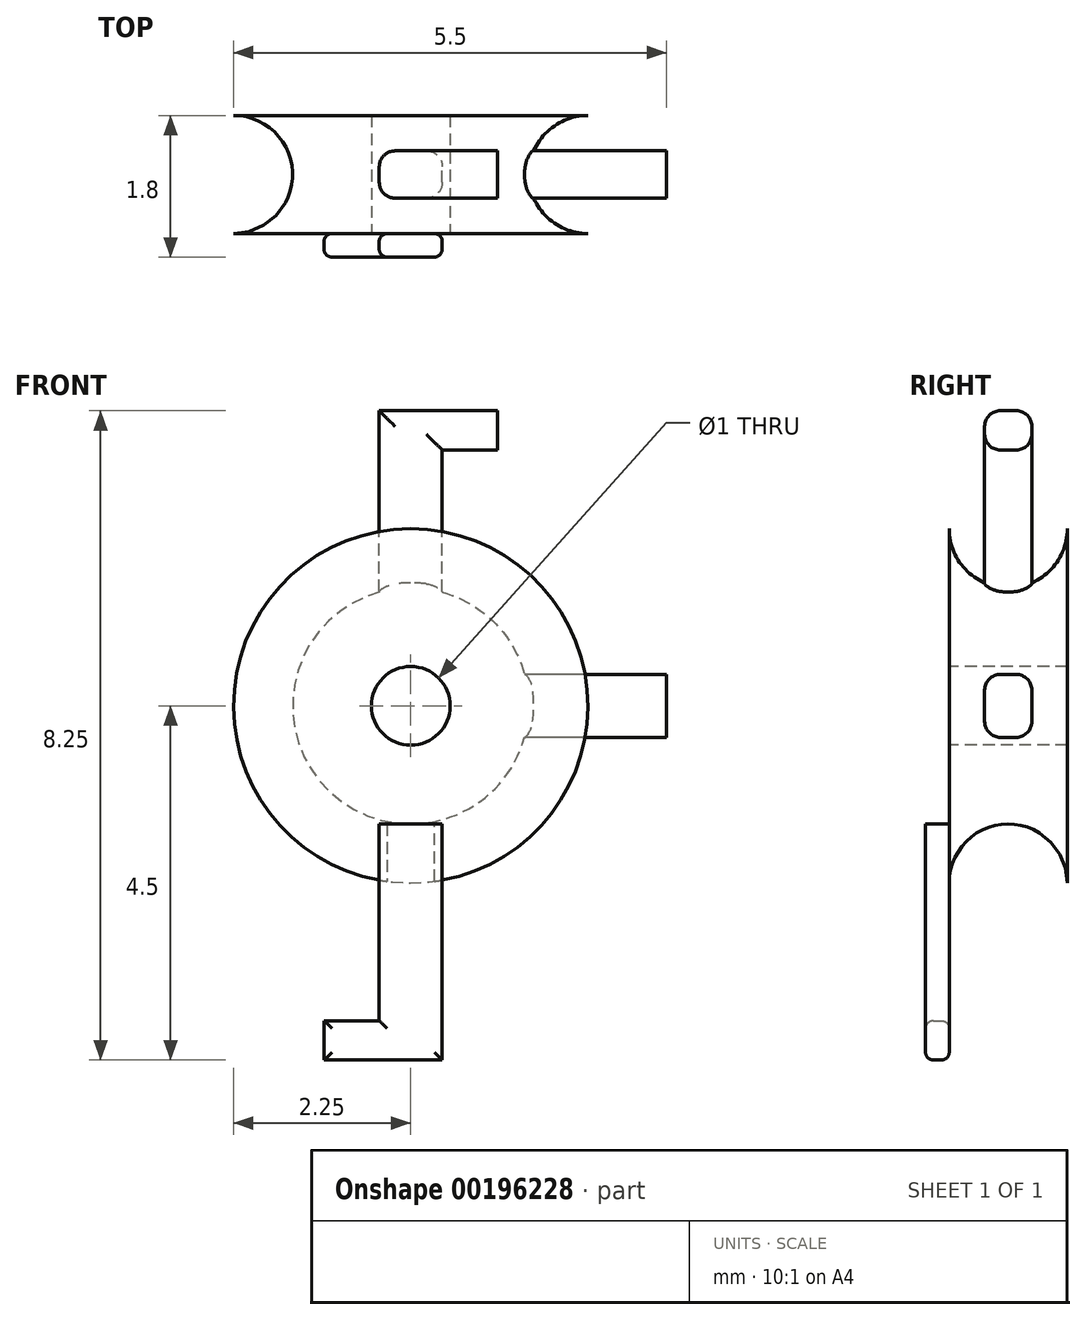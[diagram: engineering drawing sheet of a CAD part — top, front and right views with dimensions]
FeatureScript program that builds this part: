
annotation { "Feature Type Name" : "Feature", "Feature Type Description" : "" }
export const myFeature = defineFeature(function(context is Context, id is Id, definition is map)
    precondition{}
    {
        {
            var Q0;
            Q0=qCreatedBy(makeId("Front.planeOp"),FACE);
            var sketch = newSketch(context, id + "F0", { "sketchPlane" : qUnion([Q0])});
            skCircle(sketch, "E0", {"center": v(0, 0) * mm, "radius": 2.25 * mm});
            skSolve(sketch);
        }
        {
            var Q0;
            Q0 = qSketchRegion(id + "F0", true);
            extrude(context, id + "F1", {"entities" : qUnion([Q0]), "depth" : 1.5 * mm});
        }
        {
            var Q0;
            Q0=qCreatedBy(makeId("Top.planeOp"),FACE);
            var sketch = newSketch(context, id + "F2", { "sketchPlane" : qUnion([Q0])});
            skLineSegment(sketch, "E1", {"start": v(-2.25, -1.5) * mm, "end": v(-2.25, 0) * mm, "construction": true});
            skCircle(sketch, "E2", {"center": v(-2.25, -0.75) * mm, "radius": 0.75 * mm});
            skSolve(sketch);
        }
        {
            var Q0;
            Q0=makeQuery(id+"F2.imprint","IMPRINT",FACE,{"disambiguationData":[TD([[makeQuery(id+"F2.imprint","IMPRINT",EDGE,{"derivedFrom":sQuery(id+"F2.wireOp",EDGE,"E2")}),1.0]])]});
            var Q1;
            Q1=makeQuery(id+"F1.opExtrude","SWEPT_FACE",FACE,{"disambiguationData":[OSD([sQuery(id+"F0.wireOp",EDGE,"E0")])]});
            revolve(context, id + "F3", {"operationType" : NewBodyOperationType.REMOVE, "entities" : qUnion([Q0]), "axis" : qUnion([Q1]), "revolveType" : RevolveType.FULL, "oppositeDirection" : true});
        }
        {
            var Q0;
            Q0=makeQuery(id+"F1.opExtrude","CAP_FACE",FACE,{"disambiguationData":[OSD([sQuery(id+"F0.wireOp",EDGE,"E0")])],"isStart":false});
            var sketch = newSketch(context, id + "F4", { "sketchPlane" : qUnion([Q0])});
            skCircle(sketch, "E3", {"center": v(0, 0) * mm, "radius": 0.5 * mm});
            skSolve(sketch);
        }
        {
            var Q0;
            Q0=makeQuery(id+"F4.imprint","IMPRINT",FACE,{"disambiguationData":[TD([[makeQuery(id+"F4.imprint","IMPRINT",EDGE,{"derivedFrom":sQuery(id+"F4.wireOp",EDGE,"E3")}),1.0]])]});
            extrude(context, id + "F5", {"entities" : qUnion([Q0]), "operationType" : NewBodyOperationType.REMOVE, "oppositeDirection" : true, "depth" : 25 * mm});
        }
        {
            var Q0;
            Q0=qCreatedBy(makeId("Front.planeOp"),FACE);
            cPlane(context, id + "F6", {"entities" : qUnion([Q0]), "cplaneType" : CPlaneType.OFFSET, "offset" : 0.75 * mm, "width" : 150 * mm, "height" : 150 * mm});
        }
        {
            var Q0;
            Q0=qCreatedBy(id+"F6.planeOp",FACE);
            var sketch = newSketch(context, id + "F7", { "sketchPlane" : qUnion([Q0])});
            skLineSegment(sketch, "E4.bottom", {"start": v(0.4, 0.75) * mm, "end": v(-0.4, 0.75) * mm});
            skLineSegment(sketch, "E4.top", {"start": v(0.4, 3.75) * mm, "end": v(-0.4, 3.75) * mm});
            skLineSegment(sketch, "E4.left", {"start": v(0.4, 0.75) * mm, "end": v(0.4, 3.25) * mm});
            skLineSegment(sketch, "E4.right", {"start": v(-0.4, 0.75) * mm, "end": v(-0.4, 3.75) * mm});
            skPoint(sketch, "E4.middle", {"position": v(0, 2.25) * mm});
            skLineSegment(sketch, "E5", {"start": v(0.4, 3.75) * mm, "end": v(1.1, 3.75) * mm});
            skLineSegment(sketch, "E6", {"start": v(1.1, 3.75) * mm, "end": v(1.1, 3.25) * mm});
            skLineSegment(sketch, "E7", {"start": v(1.1, 3.25) * mm, "end": v(0.4, 3.25) * mm});
            skSolve(sketch);
        }
        {
            var Q0;
            Q0 = qSketchRegion(id + "F7", true);
            extrude(context, id + "F8", {"entities" : qUnion([Q0]), "operationType" : NewBodyOperationType.ADD, "depth" : 0.3 * mm, "hasSecondDirection" : true, "secondDirectionOppositeDirection" : true, "secondDirectionDepth" : 0.3 * mm});
        }
        {
            var Q0;
            Q0=makeQuery(id+"F8.opExtrude","CAP_EDGE",EDGE,{"disambiguationData":[OSD([sQuery(id+"F7.wireOp",EDGE,"E4.right")])],"isStart":false});
            var Q1;
            Q1=makeQuery(id+"F8.opExtrude","CAP_EDGE",EDGE,{"disambiguationData":[OSD([sQuery(id+"F7.wireOp",EDGE,"E4.top"),sQuery(id+"F7.wireOp",EDGE,"E5")])],"isStart":false});
            var Q2;
            Q2=makeQuery(id+"F8.opExtrude","CAP_EDGE",EDGE,{"disambiguationData":[OSD([sQuery(id+"F7.wireOp",EDGE,"E4.right")])],"isStart":true});
            var Q3;
            Q3=makeQuery(id+"F8.opExtrude","CAP_EDGE",EDGE,{"disambiguationData":[OSD([sQuery(id+"F7.wireOp",EDGE,"E4.top"),sQuery(id+"F7.wireOp",EDGE,"E5")])],"isStart":true});
            var Q4;
            Q4=makeQuery(id+"F8.opExtrude","CAP_EDGE",EDGE,{"disambiguationData":[OSD([sQuery(id+"F7.wireOp",EDGE,"E7")])],"isStart":false});
            var Q5;
            Q5=makeQuery(id+"F8.opExtrude","CAP_EDGE",EDGE,{"disambiguationData":[OSD([sQuery(id+"F7.wireOp",EDGE,"E4.left")])],"isStart":false});
            var Q6;
            Q6=makeQuery(id+"F8.opExtrude","CAP_EDGE",EDGE,{"disambiguationData":[OSD([sQuery(id+"F7.wireOp",EDGE,"E7")])],"isStart":true});
            var Q7;
            Q7=makeQuery(id+"F8.opExtrude","CAP_EDGE",EDGE,{"disambiguationData":[OSD([sQuery(id+"F7.wireOp",EDGE,"E4.left")])],"isStart":true});
            fillet(context, id + "F9", {"entities" : qUnion([Q0, Q1, Q2, Q3, Q4, Q5, Q6, Q7]), "radius" : 0.2 * mm, "tangentPropagation" : true, "allowEdgeOverflow" : false});
        }
        {
            var Q0;
            Q0=makeQuery(id+"F1.opExtrude","CAP_FACE",FACE,{"disambiguationData":[OSD([sQuery(id+"F0.wireOp",EDGE,"E0")])],"isStart":false});
            var sketch = newSketch(context, id + "F10", { "sketchPlane" : qUnion([Q0])});
            skLineSegment(sketch, "E8.bottom", {"start": v(0.4, -1.5) * mm, "end": v(-0.4, -1.5) * mm});
            skLineSegment(sketch, "E8.top", {"start": v(0.4, -4.5) * mm, "end": v(-0.4, -4.5) * mm});
            skLineSegment(sketch, "E8.left", {"start": v(0.4, -1.5) * mm, "end": v(0.4, -4.5) * mm});
            skLineSegment(sketch, "E8.right", {"start": v(-0.4, -1.5) * mm, "end": v(-0.4, -4) * mm});
            skPoint(sketch, "E8.middle", {"position": v(0, -3) * mm});
            skLineSegment(sketch, "E9", {"start": v(-0.4, -4.5) * mm, "end": v(-1.1, -4.5) * mm});
            skLineSegment(sketch, "E10", {"start": v(-1.1, -4.5) * mm, "end": v(-1.1, -4) * mm});
            skLineSegment(sketch, "E11", {"start": v(-1.1, -4) * mm, "end": v(-0.4, -4) * mm});
            skSolve(sketch);
        }
        {
            var Q0;
            {var subQ0=sQuery(id+"F10.wireOp",EDGE,"E8.top");Q0=makeQuery(id+"F10.imprint","IMPRINT",FACE,{"disambiguationData":[TD([[makeQuery(id+"F10.imprint","IMPRINT",EDGE,{"derivedFrom":subQ0}),-1.0]])]});}
            var Q1;
            {var subQ0=sQuery(id+"F10.wireOp",EDGE,"E8.bottom");Q1=makeQuery(id+"F10.imprint","IMPRINT",FACE,{"disambiguationData":[TD([[makeQuery(id+"F10.imprint","IMPRINT",EDGE,{"derivedFrom":subQ0}),1.0]])]});}
            extrude(context, id + "F11", {"entities" : qUnion([Q0, Q1]), "operationType" : NewBodyOperationType.ADD, "depth" : 0.3 * mm});
        }
        {
            var Q0;
            Q0=makeQuery(id+"F11.opExtrude","CAP_EDGE",EDGE,{"disambiguationData":[OSD([sQuery(id+"F10.wireOp",EDGE,"E8.right")])],"isStart":false});
            var Q1;
            Q1=makeQuery(id+"F11.opExtrude","CAP_EDGE",EDGE,{"disambiguationData":[OSD([sQuery(id+"F10.wireOp",EDGE,"E8.left")])],"isStart":false});
            var Q2;
            Q2=makeQuery(id+"F11.opExtrude","CAP_EDGE",EDGE,{"disambiguationData":[OSD([sQuery(id+"F10.wireOp",EDGE,"E8.top"),sQuery(id+"F10.wireOp",EDGE,"E9")])],"isStart":false});
            var Q3;
            Q3=makeQuery(id+"F11.opExtrude","CAP_EDGE",EDGE,{"disambiguationData":[OSD([sQuery(id+"F10.wireOp",EDGE,"E10")])],"isStart":false});
            var Q4;
            Q4=makeQuery(id+"F11.opExtrude","CAP_EDGE",EDGE,{"disambiguationData":[OSD([sQuery(id+"F10.wireOp",EDGE,"E11")])],"isStart":false});
            var Q5;
            {var subQ0=sQuery(id+"F10.wireOp",EDGE,"E8.right");var subQ1=sQuery(id+"F10.wireOp",EDGE,"E11");Q5=makeQuery(id+"F11.boolean.opBoolean","SPLIT",EDGE,{"disambiguationData":[TD([makeQuery(id+"F11.opExtrude","SWEPT_FACE",FACE,{"disambiguationData":[OSD([subQ1])]})])],"derivedFrom":makeQuery(id+"F11.opExtrude","CAP_EDGE",EDGE,{"disambiguationData":[OSD([subQ0])],"isStart":true})});}
            var Q6;
            Q6=makeQuery(id+"F11.opExtrude","CAP_EDGE",EDGE,{"disambiguationData":[OSD([sQuery(id+"F10.wireOp",EDGE,"E10")])],"isStart":true});
            var Q7;
            Q7=makeQuery(id+"F11.opExtrude","CAP_EDGE",EDGE,{"disambiguationData":[OSD([sQuery(id+"F10.wireOp",EDGE,"E11")])],"isStart":true});
            var Q8;
            Q8=makeQuery(id+"F11.opExtrude","CAP_EDGE",EDGE,{"disambiguationData":[OSD([sQuery(id+"F10.wireOp",EDGE,"E8.top"),sQuery(id+"F10.wireOp",EDGE,"E9")])],"isStart":true});
            var Q9;
            {var subQ0=sQuery(id+"F10.wireOp",EDGE,"E9");var subQ1=sQuery(id+"F10.wireOp",EDGE,"E8.top");var subQ2=sQuery(id+"F10.wireOp",EDGE,"E8.left");Q9=makeQuery(id+"F11.boolean.opBoolean","SPLIT",EDGE,{"disambiguationData":[TD([makeQuery(id+"F11.opExtrude","SWEPT_FACE",FACE,{"disambiguationData":[OSD([subQ1,subQ0])]})])],"derivedFrom":makeQuery(id+"F11.opExtrude","CAP_EDGE",EDGE,{"disambiguationData":[OSD([subQ2])],"isStart":true})});}
            fillet(context, id + "F12", {"entities" : qUnion([Q0, Q1, Q2, Q3, Q4, Q5, Q6, Q7, Q8, Q9]), "radius" : 0.1 * mm, "tangentPropagation" : true, "allowEdgeOverflow" : false});
        }
        {
            var Q0;
            Q0=qCreatedBy(id+"F6.planeOp",FACE);
            var sketch = newSketch(context, id + "F13", { "sketchPlane" : qUnion([Q0])});
            skLineSegment(sketch, "E12.bottom", {"start": v(3.25, -0.4) * mm, "end": v(1.25, -0.4) * mm});
            skLineSegment(sketch, "E12.top", {"start": v(3.25, 0.4) * mm, "end": v(1.25, 0.4) * mm});
            skLineSegment(sketch, "E12.left", {"start": v(3.25, -0.4) * mm, "end": v(3.25, 0.4) * mm});
            skLineSegment(sketch, "E12.right", {"start": v(1.25, -0.4) * mm, "end": v(1.25, 0.4) * mm});
            skPoint(sketch, "E12.middle", {"position": v(2.25, 0) * mm});
            skSolve(sketch);
        }
        {
            var Q0;
            Q0 = qSketchRegion(id + "F13", true);
            extrude(context, id + "F14", {"entities" : qUnion([Q0]), "operationType" : NewBodyOperationType.ADD, "depth" : 0.3 * mm, "hasSecondDirection" : true, "secondDirectionOppositeDirection" : true, "secondDirectionDepth" : 0.3 * mm});
        }
        {
            var Q0;
            Q0=makeQuery(id+"F14.opExtrude","CAP_EDGE",EDGE,{"disambiguationData":[OSD([sQuery(id+"F13.wireOp",EDGE,"E12.top")])],"isStart":false});
            var Q1;
            Q1=makeQuery(id+"F14.opExtrude","CAP_EDGE",EDGE,{"disambiguationData":[OSD([sQuery(id+"F13.wireOp",EDGE,"E12.bottom")])],"isStart":false});
            var Q2;
            Q2=makeQuery(id+"F14.opExtrude","CAP_EDGE",EDGE,{"disambiguationData":[OSD([sQuery(id+"F13.wireOp",EDGE,"E12.bottom")])],"isStart":true});
            var Q3;
            Q3=makeQuery(id+"F14.opExtrude","CAP_EDGE",EDGE,{"disambiguationData":[OSD([sQuery(id+"F13.wireOp",EDGE,"E12.top")])],"isStart":true});
            fillet(context, id + "F15", {"entities" : qUnion([Q0, Q1, Q2, Q3]), "radius" : 0.2 * mm, "tangentPropagation" : true, "allowEdgeOverflow" : false});
        }
    });
